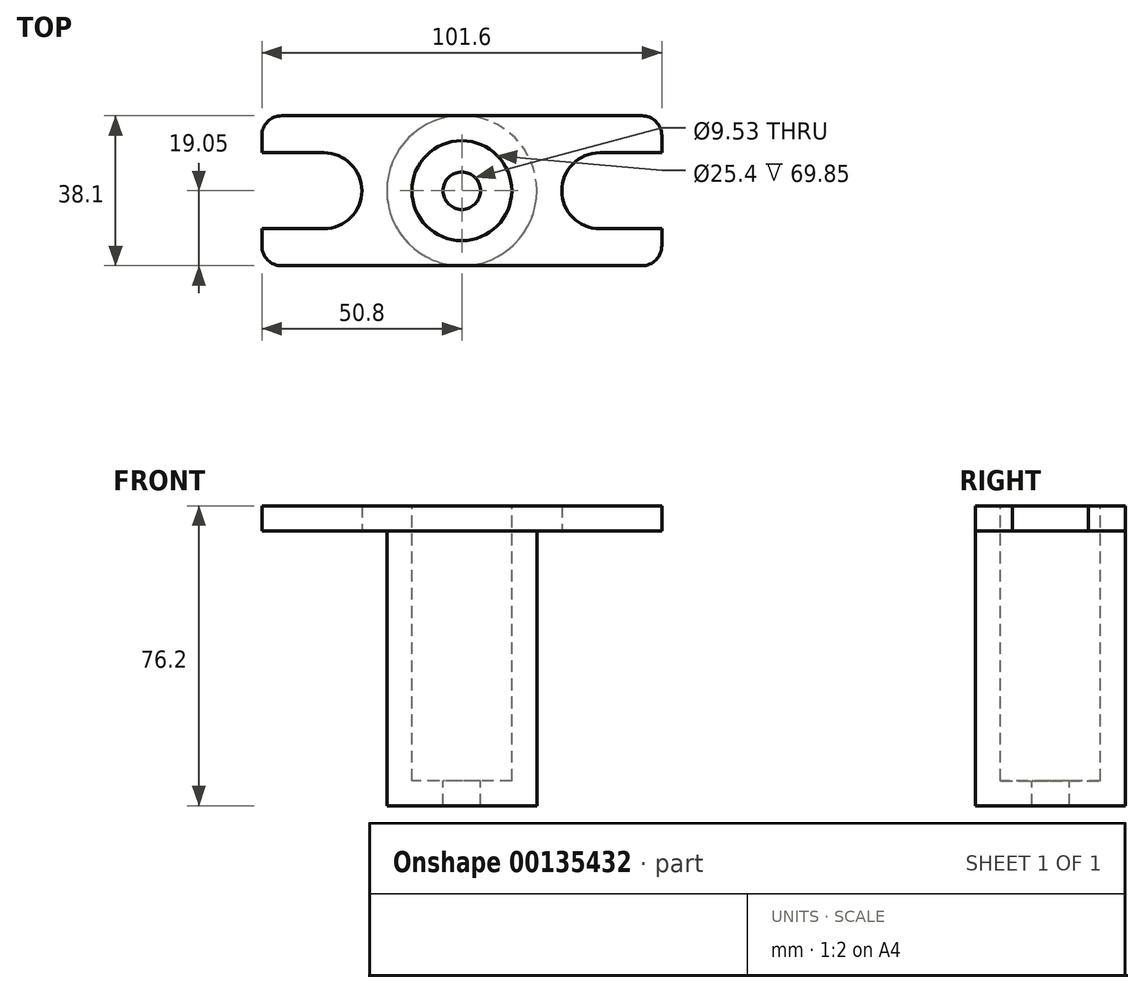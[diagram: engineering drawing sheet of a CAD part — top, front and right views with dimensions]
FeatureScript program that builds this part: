
annotation { "Feature Type Name" : "Feature", "Feature Type Description" : "" }
export const myFeature = defineFeature(function(context is Context, id is Id, definition is map)
    precondition{}
    {
        {
            var Q0;
            Q0=qCreatedBy(makeId("Top.planeOp"),FACE);
            var sketch = newSketch(context, id + "F0", { "sketchPlane" : qUnion([Q0])});
            skLineSegment(sketch, "E0", {"start": v(0, 0) * mm, "end": v(101.6, 0) * mm});
            skLineSegment(sketch, "E1", {"start": v(101.6, 0) * mm, "end": v(101.6, 9.4) * mm});
            skLineSegment(sketch, "E2", {"start": v(101.6, 9.4) * mm, "end": v(85.85, 9.4) * mm});
            skLineSegment(sketch, "E3", {"start": v(85.85, 28.7) * mm, "end": v(101.6, 28.7) * mm});
            skLineSegment(sketch, "E4", {"start": v(101.6, 28.7) * mm, "end": v(101.6, 38.1) * mm});
            skLineSegment(sketch, "E5", {"start": v(101.6, 38.1) * mm, "end": v(0, 38.1) * mm});
            skLineSegment(sketch, "E6", {"start": v(0, 38.1) * mm, "end": v(0, 28.7) * mm});
            skLineSegment(sketch, "E7", {"start": v(0, 28.7) * mm, "end": v(15.75, 28.7) * mm});
            skLineSegment(sketch, "E8", {"start": v(15.75, 9.4) * mm, "end": v(0, 9.4) * mm});
            skLineSegment(sketch, "E9", {"start": v(0, 9.4) * mm, "end": v(0, 0) * mm});
            skArc(sketch, "E10", {"start": v(15.75, 9.4) * mm, "mid": v(25.4, 19.05) * mm, "end": v(15.75, 28.7) * mm});
            skArc(sketch, "E11", {"start": v(85.85, 28.7) * mm, "mid": v(76.2, 19.05) * mm, "end": v(85.85, 9.4) * mm});
            skCircle(sketch, "E12", {"center": v(50.8, 19.05) * mm, "radius": 12.7 * mm, "construction": true});
            skSolve(sketch);
        }
        {
            var Q0;
            Q0 = qSketchRegion(id + "F0", true);
            extrude(context, id + "F1", {"entities" : qUnion([Q0]), "depth" : 6.35 * mm});
        }
        {
            var Q0;
            Q0=qCreatedBy(makeId("Top.planeOp"),FACE);
            var sketch = newSketch(context, id + "F2", { "sketchPlane" : qUnion([Q0])});
            skCircle(sketch, "E13", {"center": v(50.8, 19.05) * mm, "radius": 19.05 * mm});
            skCircle(sketch, "E14", {"center": v(50.8, 19.05) * mm, "radius": 4.76 * mm});
            skSolve(sketch);
        }
        {
            var Q0;
            Q0=qCreatedBy(makeId("Top.planeOp"),FACE);
            var sketch = newSketch(context, id + "F3", { "sketchPlane" : qUnion([Q0])});
            skCircle(sketch, "E15", {"center": v(50.8, 19.05) * mm, "radius": 12.7 * mm});
            skSolve(sketch);
        }
        {
            var Q0;
            Q0 = qSketchRegion(id + "F2", true);
            extrude(context, id + "F4", {"entities" : qUnion([Q0]), "operationType" : NewBodyOperationType.ADD, "oppositeDirection" : true, "depth" : 69.85 * mm});
        }
        {
            var Q0;
            Q0 = qSketchRegion(id + "F3", true);
            extrude(context, id + "F5", {"entities" : qUnion([Q0]), "operationType" : NewBodyOperationType.REMOVE, "oppositeDirection" : true, "depth" : 63.5 * mm, "hasSecondDirection" : true, "secondDirectionOppositeDirection" : false, "secondDirectionDepth" : 25.4 * mm});
        }
        {
            var Q0;
            Q0=makeQuery(id+"F1.opExtrude","SWEPT_EDGE",EDGE,{"disambiguationData":[OSD([sQuery(id+"F0.wireOp",EDGE,"E0"),sQuery(id+"F0.wireOp",EDGE,"E1")])]});
            var Q1;
            Q1=makeQuery(id+"F1.opExtrude","SWEPT_EDGE",EDGE,{"disambiguationData":[OSD([sQuery(id+"F0.wireOp",EDGE,"E4"),sQuery(id+"F0.wireOp",EDGE,"E5")])]});
            var Q2;
            Q2=makeQuery(id+"F1.opExtrude","SWEPT_EDGE",EDGE,{"disambiguationData":[OSD([sQuery(id+"F0.wireOp",EDGE,"E0"),sQuery(id+"F0.wireOp",EDGE,"E9")])]});
            var Q3;
            Q3=makeQuery(id+"F1.opExtrude","SWEPT_EDGE",EDGE,{"disambiguationData":[OSD([sQuery(id+"F0.wireOp",EDGE,"E5"),sQuery(id+"F0.wireOp",EDGE,"E6")])]});
            fillet(context, id + "F6", {"entities" : qUnion([Q0, Q1, Q2, Q3]), "radius" : 5.08 * mm, "tangentPropagation" : true, "allowEdgeOverflow" : false});
        }
    });
